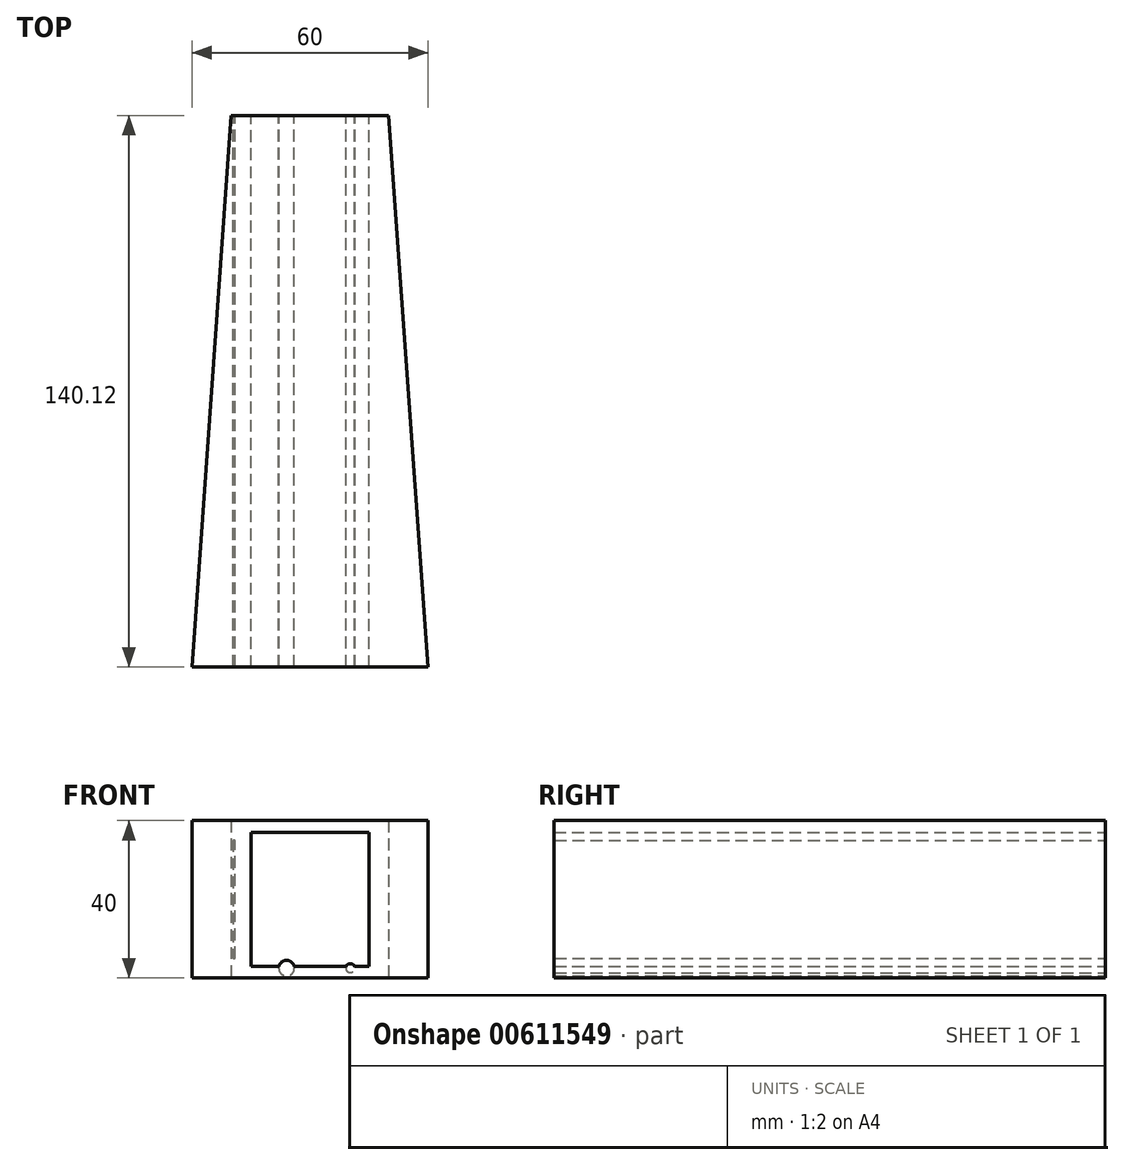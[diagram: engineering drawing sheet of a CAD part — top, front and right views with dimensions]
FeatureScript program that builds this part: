
annotation { "Feature Type Name" : "Feature", "Feature Type Description" : "" }
export const myFeature = defineFeature(function(context is Context, id is Id, definition is map)
    precondition{}
    {
        {
            var Q0;
            Q0=qCreatedBy(makeId("Front.planeOp"),FACE);
            var sketch = newSketch(context, id + "F0", { "sketchPlane" : qUnion([Q0])});
            skLineSegment(sketch, "E0.bottom", {"start": v(-15, 20) * mm, "end": v(15, 20) * mm});
            skLineSegment(sketch, "E0.top", {"start": v(-15, -20) * mm, "end": v(15, -20) * mm});
            skLineSegment(sketch, "E0.left", {"start": v(-20, 15) * mm, "end": v(-20, -15) * mm});
            skLineSegment(sketch, "E0.right", {"start": v(20, 15) * mm, "end": v(20, -15) * mm});
            skPoint(sketch, "E0.middle", {"position": v(0, 0) * mm});
            skPoint(sketch, "E1.visualSharp", {"position": v(-20, -20) * mm});
            skPoint(sketch, "E2.visualSharp", {"position": v(20, -20) * mm});
            skLineSegment(sketch, "E3", {"start": v(-20, -15) * mm, "end": v(20, -15) * mm});
            skLineSegment(sketch, "E4", {"start": v(-20, -15) * mm, "end": v(-20, -11.86) * mm});
            skLineSegment(sketch, "E5", {"start": v(-20, -15) * mm, "end": v(-19, -15) * mm});
            skLineSegment(sketch, "E6", {"start": v(-19, -15) * mm, "end": v(-19, 20) * mm});
            skLineSegment(sketch, "E7", {"start": v(-19, 20) * mm, "end": v(-19, 15) * mm});
            skLineSegment(sketch, "E8", {"start": v(-19, 15) * mm, "end": v(-20, 15) * mm});
            skLineSegment(sketch, "E9.MirrorCS", {"start": v(19, -15) * mm, "end": v(19, 20) * mm});
            skLineSegment(sketch, "E10.MirrorCS", {"start": v(20, 20) * mm, "end": v(20, -15) * mm});
            skLineSegment(sketch, "E11.MirrorCS", {"start": v(19, 15) * mm, "end": v(20, 15) * mm});
            skLineSegment(sketch, "E12", {"start": v(-19.5, 15) * mm, "end": v(-19.5, -15) * mm});
            skLineSegment(sketch, "E13", {"start": v(-19.5, -5.26) * mm, "end": v(-19.5, -3.26) * mm});
            skLineSegment(sketch, "E14", {"start": v(-19.5, 2.74) * mm, "end": v(-19.5, 4.74) * mm});
            skLineSegment(sketch, "E15", {"start": v(-15, -20) * mm, "end": v(-15, -15) * mm});
            skLineSegment(sketch, "E16", {"start": v(-15, -17.5) * mm, "end": v(15, -17.5) * mm});
            skLineSegment(sketch, "E17", {"start": v(15, -17.5) * mm, "end": v(15, -20) * mm});
            skLineSegment(sketch, "E18", {"start": v(15, -17.5) * mm, "end": v(15, -15) * mm});
            skLineSegment(sketch, "E19", {"start": v(-15, -15) * mm, "end": v(-18.54, -18.54) * mm});
            skLineSegment(sketch, "E20", {"start": v(-18.54, -18.54) * mm, "end": v(-16.77, -16.77) * mm});
            skLineSegment(sketch, "E21", {"start": v(-20, -15) * mm, "end": v(-15, -20) * mm});
            skCircle(sketch, "E22", {"center": v(-10.25, -17.5) * mm, "radius": 1.14 * mm});
            skCircle(sketch, "E23", {"center": v(-5.95, -17.5) * mm, "radius": 1.97 * mm});
            skCircle(sketch, "E24.MirrorC", {"center": v(5.95, -17.5) * mm, "radius": 1.97 * mm});
            skCircle(sketch, "E25.MirrorC", {"center": v(10.25, -17.5) * mm, "radius": 1.14 * mm});
            skLineSegment(sketch, "E26", {"start": v(-19, 20) * mm, "end": v(19, 20) * mm});
            skPoint(sketch, "E27.visualSharp", {"position": v(-20, 20) * mm});
            skPoint(sketch, "E28.visualSharp", {"position": v(20, 20) * mm});
            skLineSegment(sketch, "E29", {"start": v(-19, 17.5) * mm, "end": v(19, 17.5) * mm});
            skLineSegment(sketch, "E30", {"start": v(-19, 18.83) * mm, "end": v(19, 18.83) * mm});
            skLineSegment(sketch, "E31", {"start": v(-20, 15) * mm, "end": v(-20, 20) * mm});
            skLineSegment(sketch, "E32", {"start": v(19, 20) * mm, "end": v(20, 20) * mm});
            skLineSegment(sketch, "E33", {"start": v(-20, 20) * mm, "end": v(-19, 20) * mm});
            skLineSegment(sketch, "E34", {"start": v(15, -20) * mm, "end": v(20, -20) * mm});
            skLineSegment(sketch, "E35", {"start": v(20, -15) * mm, "end": v(20, -20) * mm});
            skLineSegment(sketch, "E36", {"start": v(-15, -20) * mm, "end": v(-20, -20) * mm});
            skLineSegment(sketch, "E37", {"start": v(-20, -15) * mm, "end": v(-20, -20) * mm});
            skSolve(sketch);
        }
        {
            var Q0;
            {var subQ1=sQuery(id+"F0.wireOp",EDGE,"E0.left");Q0=makeQuery(id+"F0.imprint","IMPRINT",FACE,{"disambiguationData":[TD([[makeQuery(id+"F0.imprint","IMPRINT",EDGE,{"derivedFrom":subQ1}),1.0]])]});}
            var Q1;
            {var subQ4=sQuery(id+"F0.wireOp",EDGE,"E6");Q1=makeQuery(id+"F0.imprint","IMPRINT",FACE,{"disambiguationData":[TD([[makeQuery(id+"F0.imprint","IMPRINT",EDGE,{"derivedFrom":subQ4}),1.0]])]});}
            var Q2;
            {var subQ3=sQuery(id+"F0.wireOp",EDGE,"E36");Q2=makeQuery(id+"F0.imprint","IMPRINT",FACE,{"disambiguationData":[TD([[makeQuery(id+"F0.imprint","IMPRINT",EDGE,{"derivedFrom":subQ3}),-1.0]])]});}
            var Q3;
            {var subQ0=sQuery(id+"F0.wireOp",EDGE,"E19");Q3=makeQuery(id+"F0.imprint","IMPRINT",FACE,{"disambiguationData":[TD([[makeQuery(id+"F0.imprint","IMPRINT",EDGE,{"derivedFrom":subQ0}),-1.0]])]});}
            var Q4;
            {var subQ1=sQuery(id+"F0.wireOp",EDGE,"E19");Q4=makeQuery(id+"F0.imprint","IMPRINT",FACE,{"disambiguationData":[TD([[makeQuery(id+"F0.imprint","IMPRINT",EDGE,{"derivedFrom":subQ1}),1.0]])]});}
            var Q5;
            {var subQ0=sQuery(id+"F0.wireOp",EDGE,"E18");Q5=makeQuery(id+"F0.imprint","IMPRINT",FACE,{"disambiguationData":[TD([[makeQuery(id+"F0.imprint","IMPRINT",EDGE,{"derivedFrom":subQ0}),1.0]])]});}
            var Q6;
            {var subQ14=sQuery(id+"F0.wireOp",EDGE,"E0.top");Q6=makeQuery(id+"F0.imprint","IMPRINT",FACE,{"disambiguationData":[TD([[makeQuery(id+"F0.imprint","IMPRINT",EDGE,{"derivedFrom":subQ14}),1.0]])]});}
            var Q7;
            {var subQ0=sQuery(id+"F0.wireOp",EDGE,"E22");var subQ1=sQuery(id+"F0.wireOp",EDGE,"E16");var subQ2=makeQuery(id+"F0.imprint","INTERSECT",VERTEX,{"disambiguationData":[OD(0.0)],"derivedFrom":[subQ1,subQ0]});Q7=makeQuery(id+"F0.imprint","IMPRINT",FACE,{"disambiguationData":[TD([[makeQuery(id+"F0.imprint","IMPRINT",EDGE,{"disambiguationData":[TD([[subQ2,-1.0]])],"derivedFrom":subQ1}),-1.0]])]});}
            var Q8;
            {var subQ0=sQuery(id+"F0.wireOp",EDGE,"E22");var subQ1=sQuery(id+"F0.wireOp",EDGE,"E16");var subQ2=makeQuery(id+"F0.imprint","INTERSECT",VERTEX,{"disambiguationData":[OD(0.0)],"derivedFrom":[subQ1,subQ0]});Q8=makeQuery(id+"F0.imprint","IMPRINT",FACE,{"disambiguationData":[TD([[makeQuery(id+"F0.imprint","IMPRINT",EDGE,{"disambiguationData":[TD([[subQ2,-1.0]])],"derivedFrom":subQ1}),1.0]])]});}
            var Q9;
            {var subQ0=sQuery(id+"F0.wireOp",EDGE,"E23");var subQ1=sQuery(id+"F0.wireOp",EDGE,"E16");var subQ2=makeQuery(id+"F0.imprint","INTERSECT",VERTEX,{"disambiguationData":[OD(0.0)],"derivedFrom":[subQ1,subQ0]});Q9=makeQuery(id+"F0.imprint","IMPRINT",FACE,{"disambiguationData":[TD([[makeQuery(id+"F0.imprint","IMPRINT",EDGE,{"disambiguationData":[TD([[subQ2,-1.0]])],"derivedFrom":subQ1}),1.0]])]});}
            var Q10;
            {var subQ0=sQuery(id+"F0.wireOp",EDGE,"E23");var subQ1=sQuery(id+"F0.wireOp",EDGE,"E16");var subQ2=makeQuery(id+"F0.imprint","INTERSECT",VERTEX,{"disambiguationData":[OD(0.0)],"derivedFrom":[subQ1,subQ0]});Q10=makeQuery(id+"F0.imprint","IMPRINT",FACE,{"disambiguationData":[TD([[makeQuery(id+"F0.imprint","IMPRINT",EDGE,{"disambiguationData":[TD([[subQ2,-1.0]])],"derivedFrom":subQ1}),-1.0]])]});}
            var Q11;
            {var subQ0=sQuery(id+"F0.wireOp",EDGE,"E24.MirrorC");var subQ1=sQuery(id+"F0.wireOp",EDGE,"E16");var subQ2=makeQuery(id+"F0.imprint","INTERSECT",VERTEX,{"disambiguationData":[OD(0.0)],"derivedFrom":[subQ1,subQ0]});Q11=makeQuery(id+"F0.imprint","IMPRINT",FACE,{"disambiguationData":[TD([[makeQuery(id+"F0.imprint","IMPRINT",EDGE,{"disambiguationData":[TD([[subQ2,-1.0]])],"derivedFrom":subQ1}),1.0]])]});}
            var Q12;
            {var subQ0=sQuery(id+"F0.wireOp",EDGE,"E24.MirrorC");var subQ1=sQuery(id+"F0.wireOp",EDGE,"E16");var subQ2=makeQuery(id+"F0.imprint","INTERSECT",VERTEX,{"disambiguationData":[OD(0.0)],"derivedFrom":[subQ1,subQ0]});Q12=makeQuery(id+"F0.imprint","IMPRINT",FACE,{"disambiguationData":[TD([[makeQuery(id+"F0.imprint","IMPRINT",EDGE,{"disambiguationData":[TD([[subQ2,-1.0]])],"derivedFrom":subQ1}),-1.0]])]});}
            var Q13;
            {var subQ0=sQuery(id+"F0.wireOp",EDGE,"E6");Q13=makeQuery(id+"F0.imprint","IMPRINT",FACE,{"disambiguationData":[TD([[makeQuery(id+"F0.imprint","IMPRINT",EDGE,{"derivedFrom":subQ0}),-1.0]])]});}
            var Q14;
            {var subQ0=sQuery(id+"F0.wireOp",EDGE,"E25.MirrorC");var subQ1=sQuery(id+"F0.wireOp",EDGE,"E16");var subQ2=makeQuery(id+"F0.imprint","INTERSECT",VERTEX,{"disambiguationData":[OD(0.0)],"derivedFrom":[subQ1,subQ0]});Q14=makeQuery(id+"F0.imprint","IMPRINT",FACE,{"disambiguationData":[TD([[makeQuery(id+"F0.imprint","IMPRINT",EDGE,{"disambiguationData":[TD([[subQ2,-1.0]])],"derivedFrom":subQ1}),-1.0]])]});}
            var Q15;
            {var subQ0=sQuery(id+"F0.wireOp",EDGE,"E25.MirrorC");var subQ1=sQuery(id+"F0.wireOp",EDGE,"E16");var subQ2=makeQuery(id+"F0.imprint","INTERSECT",VERTEX,{"disambiguationData":[OD(0.0)],"derivedFrom":[subQ1,subQ0]});Q15=makeQuery(id+"F0.imprint","IMPRINT",FACE,{"disambiguationData":[TD([[makeQuery(id+"F0.imprint","IMPRINT",EDGE,{"disambiguationData":[TD([[subQ2,-1.0]])],"derivedFrom":subQ1}),1.0]])]});}
            var Q16;
            Q16=makeQuery(id+"F0.imprint","IMPRINT",FACE,{"disambiguationData":[TD([[makeQuery(id+"F0.imprint","IMPRINT",EDGE,{"derivedFrom":sQuery(id+"F0.wireOp",EDGE,"E17")}),1.0]])]});
            var Q17;
            {var subQ5=sQuery(id+"F0.wireOp",EDGE,"E11.MirrorCS");Q17=makeQuery(id+"F0.imprint","IMPRINT",FACE,{"disambiguationData":[TD([[makeQuery(id+"F0.imprint","IMPRINT",EDGE,{"derivedFrom":subQ5}),-1.0]])]});}
            var Q18;
            {var subQ7=sQuery(id+"F0.wireOp",EDGE,"E31");Q18=makeQuery(id+"F0.imprint","IMPRINT",FACE,{"disambiguationData":[TD([[makeQuery(id+"F0.imprint","IMPRINT",EDGE,{"derivedFrom":subQ7}),-1.0]])]});}
            var Q19;
            {var subQ0=sQuery(id+"F0.wireOp",EDGE,"E29");Q19=makeQuery(id+"F0.imprint","IMPRINT",FACE,{"disambiguationData":[TD([[makeQuery(id+"F0.imprint","IMPRINT",EDGE,{"derivedFrom":subQ0}),1.0]])]});}
            var Q20;
            {var subQ3=sQuery(id+"F0.wireOp",EDGE,"E30");Q20=makeQuery(id+"F0.imprint","IMPRINT",FACE,{"disambiguationData":[TD([[makeQuery(id+"F0.imprint","IMPRINT",EDGE,{"derivedFrom":subQ3}),1.0]])]});}
            var Q21;
            {var subQ2=sQuery(id+"F0.wireOp",EDGE,"E11.MirrorCS");Q21=makeQuery(id+"F0.imprint","IMPRINT",FACE,{"disambiguationData":[TD([[makeQuery(id+"F0.imprint","IMPRINT",EDGE,{"derivedFrom":subQ2}),1.0]])]});}
            extrude(context, id + "F1", {"entities" : qUnion([Q0, Q1, Q2, Q3, Q4, Q5, Q6, Q7, Q8, Q9, Q10, Q11, Q12, Q13, Q14, Q15, Q16, Q17, Q18, Q19, Q20, Q21]), "depth" : 140 * mm, "offsetDistance" : 25 * mm});
        }
        {
            var Q0;
            Q0=makeQuery(id+"F1.opExtrude","SWEPT_FACE",FACE,{"disambiguationData":[OSD([sQuery(id+"F0.wireOp",EDGE,"E26"),sQuery(id+"F0.wireOp",EDGE,"E32"),sQuery(id+"F0.wireOp",EDGE,"E33")])]});
            var sketch = newSketch(context, id + "F2", { "sketchPlane" : qUnion([Q0])});
            skLineSegment(sketch, "E38.bottom", {"start": v(20, -140) * mm, "end": v(-20, -140) * mm});
            skLineSegment(sketch, "E38.top", {"start": v(20, -140.12) * mm, "end": v(-20, -140.12) * mm});
            skLineSegment(sketch, "E38.left", {"start": v(20, -140) * mm, "end": v(20, -140.12) * mm});
            skLineSegment(sketch, "E38.right", {"start": v(-20, -140) * mm, "end": v(-20, -140.12) * mm});
            skLineSegment(sketch, "E39", {"start": v(-20, -140.12) * mm, "end": v(-30, -140.12) * mm});
            skLineSegment(sketch, "E40", {"start": v(-30, -140.12) * mm, "end": v(-20, 0) * mm});
            skLineSegment(sketch, "E41.MirrorCS", {"start": v(30, -140.12) * mm, "end": v(20, 0) * mm});
            skLineSegment(sketch, "E42.MirrorCS", {"start": v(20, -140.12) * mm, "end": v(30, -140.12) * mm});
            skSolve(sketch);
        }
        {
            var Q0;
            Q0 = qSketchRegion(id + "F2", true);
            var Q1;
            Q1=makeQuery(id+"F2.imprint","IMPRINT",FACE,{"disambiguationData":[TD([[makeQuery(id+"F2.imprint","IMPRINT",EDGE,{"derivedFrom":sQuery(id+"F2.wireOp",EDGE,"E38.right")}),-1.0]])]});
            var Q2;
            Q2=makeQuery(id+"F2.imprint","IMPRINT",FACE,{"disambiguationData":[TD([[makeQuery(id+"F2.imprint","IMPRINT",EDGE,{"derivedFrom":sQuery(id+"F2.wireOp",EDGE,"E38.left")}),1.0]])]});
            var Q3;
            Q3=makeQuery(id+"F1.opExtrude","SWEPT_FACE",FACE,{"disambiguationData":[OSD([sQuery(id+"F0.wireOp",EDGE,"E0.top"),sQuery(id+"F0.wireOp",EDGE,"E34"),sQuery(id+"F0.wireOp",EDGE,"E36")])]});
            extrude(context, id + "F3", {"entities" : qUnion([Q0, Q1, Q2]), "operationType" : NewBodyOperationType.ADD, "endBound" : BoundingType.UP_TO_SURFACE, "oppositeDirection" : true, "depth" : 25 * mm, "endBoundEntityFace" : qUnion([Q3]), "offsetDistance" : 25 * mm});
        }
        {
            var Q0;
            Q0=makeQuery(id+"F1.opExtrude","CAP_FACE",FACE,{"disambiguationData":[OSD([sQuery(id+"F0.wireOp",EDGE,"E0.top"),sQuery(id+"F0.wireOp",EDGE,"E0.left"),sQuery(id+"F0.wireOp",EDGE,"E4"),sQuery(id+"F0.wireOp",EDGE,"E10.MirrorCS"),sQuery(id+"F0.wireOp",EDGE,"E26"),sQuery(id+"F0.wireOp",EDGE,"E31"),sQuery(id+"F0.wireOp",EDGE,"E32"),sQuery(id+"F0.wireOp",EDGE,"E33"),sQuery(id+"F0.wireOp",EDGE,"E34"),sQuery(id+"F0.wireOp",EDGE,"E35"),sQuery(id+"F0.wireOp",EDGE,"E36"),sQuery(id+"F0.wireOp",EDGE,"E37")])],"isStart":true});
            var sketch = newSketch(context, id + "F4", { "sketchPlane" : qUnion([Q0])});
            skLineSegment(sketch, "E43.bottom", {"start": v(-15, -17) * mm, "end": v(15, -17) * mm});
            skLineSegment(sketch, "E43.top", {"start": v(-15, 17) * mm, "end": v(15, 17) * mm});
            skLineSegment(sketch, "E43.left", {"start": v(-15, -17) * mm, "end": v(-15, 17) * mm});
            skLineSegment(sketch, "E43.right", {"start": v(15, -17) * mm, "end": v(15, 17) * mm});
            skPoint(sketch, "E43.middle", {"position": v(0, 0) * mm});
            skSolve(sketch);
        }
        {
            var Q0;
            Q0=makeQuery(id+"F4.imprint","IMPRINT",FACE,{"disambiguationData":[TD([[makeQuery(id+"F4.imprint","IMPRINT",EDGE,{"derivedFrom":sQuery(id+"F4.wireOp",EDGE,"E43.bottom")}),1.0]])]});
            var Q1;
            Q1=makeQuery(id+"F3.opExtrude","SWEPT_FACE",FACE,{"disambiguationData":[OSD([sQuery(id+"F2.wireOp",EDGE,"E38.top"),sQuery(id+"F2.wireOp",EDGE,"E39"),sQuery(id+"F2.wireOp",EDGE,"E42.MirrorCS")])]});
            extrude(context, id + "F5", {"entities" : qUnion([Q0]), "operationType" : NewBodyOperationType.REMOVE, "endBound" : BoundingType.UP_TO_SURFACE, "oppositeDirection" : true, "depth" : 25 * mm, "endBoundEntityFace" : qUnion([Q1]), "offsetDistance" : 25 * mm});
        }
    });
